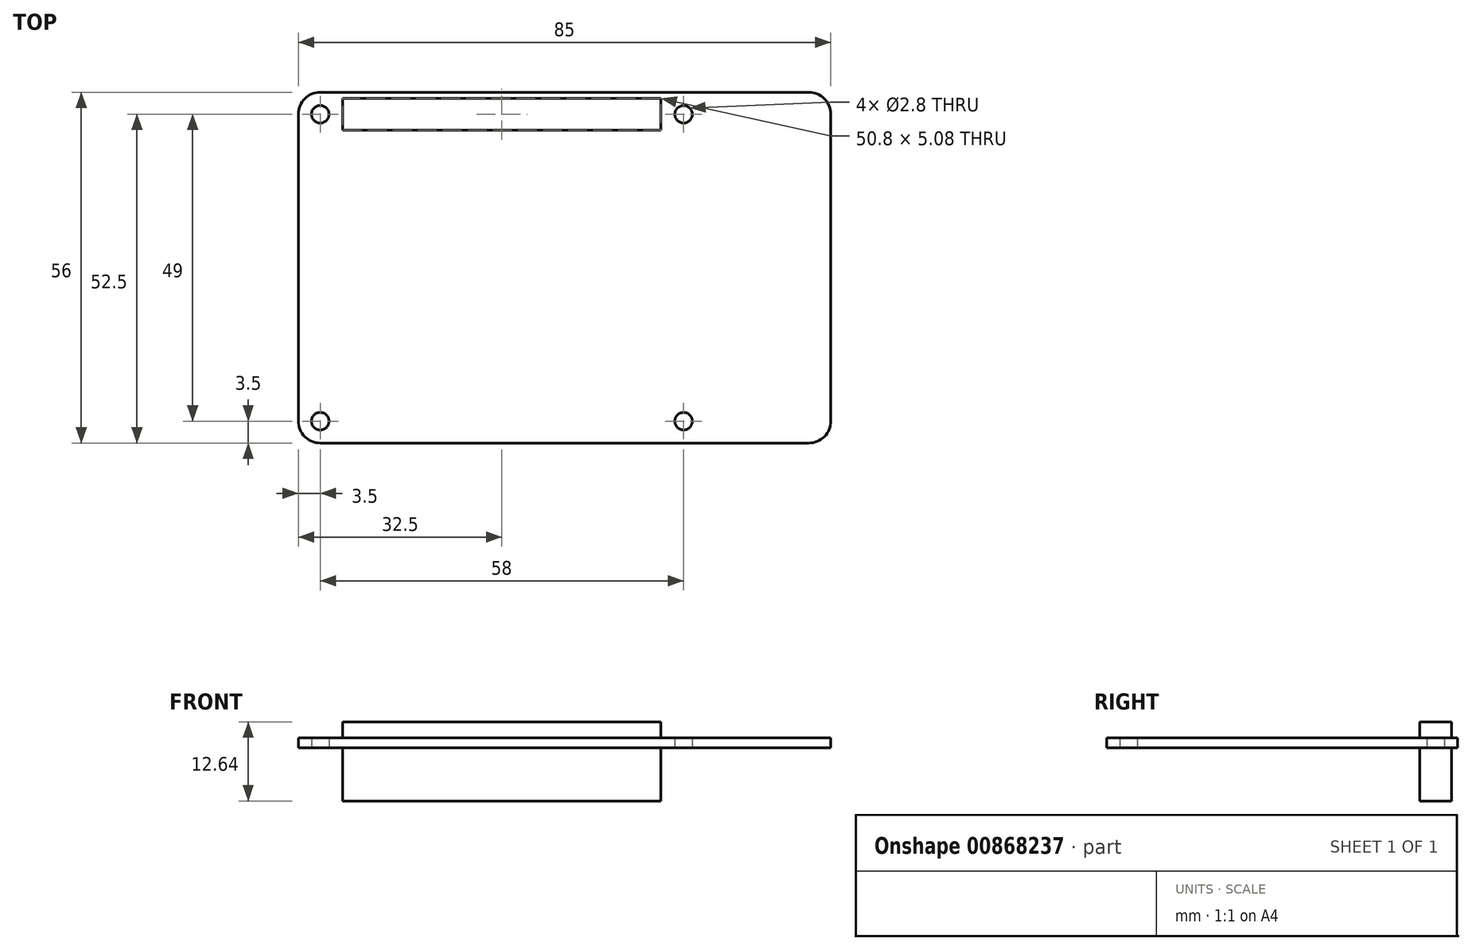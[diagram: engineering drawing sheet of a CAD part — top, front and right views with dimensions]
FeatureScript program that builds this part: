
annotation { "Feature Type Name" : "Feature", "Feature Type Description" : "" }
export const myFeature = defineFeature(function(context is Context, id is Id, definition is map)
    precondition{}
    {
        {
            var Q0;
            Q0=qCreatedBy(makeId("Top.planeOp"),FACE);
            var sketch = newSketch(context, id + "F0", { "sketchPlane" : qUnion([Q0])});
            skPoint(sketch, "E0.middle", {"position": v(0, 0) * mm});
            skLineSegment(sketch, "E1.bottom", {"start": v(29, -24.5) * mm, "end": v(-29, -24.5) * mm, "construction": true});
            skLineSegment(sketch, "E1.top", {"start": v(29, 24.5) * mm, "end": v(-29, 24.5) * mm, "construction": true});
            skLineSegment(sketch, "E1.left", {"start": v(29, -24.5) * mm, "end": v(29, 24.5) * mm, "construction": true});
            skLineSegment(sketch, "E1.right", {"start": v(-29, -24.5) * mm, "end": v(-29, 24.5) * mm, "construction": true});
            skLineSegment(sketch, "E2.bottom", {"start": v(-32.5, 28) * mm, "end": v(52.5, 28) * mm});
            skLineSegment(sketch, "E2.top", {"start": v(-32.5, -28) * mm, "end": v(52.5, -28) * mm});
            skLineSegment(sketch, "E2.left", {"start": v(-32.5, 28) * mm, "end": v(-32.5, -28) * mm});
            skLineSegment(sketch, "E2.right", {"start": v(52.5, 28) * mm, "end": v(52.5, -28) * mm});
            skSolve(sketch);
        }
        {
            var Q0;
            Q0=qSketchRegion(id+"F0",true);
            extrude(context, id + "F1", {"entities" : qUnion([Q0]), "depth" : 1.6 * mm, "offsetDistance" : 25 * mm});
        }
        {
            var Q0;
            Q0=sQuery(id+"F0.wireOp",VERTEX,"E1.top.end");
            var Q1;
            Q1=sQuery(id+"F0.wireOp",VERTEX,"E1.top.start");
            var Q2;
            Q2=sQuery(id+"F0.wireOp",VERTEX,"E1.bottom.start");
            var Q3;
            Q3=sQuery(id+"F0.wireOp",VERTEX,"E1.bottom.end");
            var Q4;
            Q4=makeQuery(id+"F1.opExtrude","SWEPT_BODY",BODY,{"disambiguationData":[OSD([sQuery(id+"F0.wireOp",EDGE,"E2.bottom"),sQuery(id+"F0.wireOp",EDGE,"E2.top"),sQuery(id+"F0.wireOp",EDGE,"E2.left"),sQuery(id+"F0.wireOp",EDGE,"E2.right")])]});
            hole(context, id + "F2", {"style" : HoleStyle.SIMPLE, "endStyle" : HoleEndStyle.THROUGH, "oppositeDirection" : true, "holeDiameter" : 2.8 * mm, "majorDiameter" : 5 * mm, "isTappedThrough" : true, "tappedDepth" : 12 * mm, "tapClearance" : 3, "locations" : qUnion([Q0, Q1, Q2, Q3]), "scope" : qUnion([Q4])});
        }
        {
            var Q0;
            Q0=makeQuery(id+"F1.opExtrude","CAP_FACE",FACE,{"disambiguationData":[OSD([sQuery(id+"F0.wireOp",EDGE,"E2.bottom"),sQuery(id+"F0.wireOp",EDGE,"E2.top"),sQuery(id+"F0.wireOp",EDGE,"E2.left"),sQuery(id+"F0.wireOp",EDGE,"E2.right")])],"isStart":true});
            var sketch = newSketch(context, id + "F3", { "sketchPlane" : qUnion([Q0])});
            skLineSegment(sketch, "E3", {"start": v(-29, -24.5) * mm, "end": v(29, -24.5) * mm, "construction": true});
            skLineSegment(sketch, "E4.bottom", {"start": v(25.4, -27.04) * mm, "end": v(-25.4, -27.04) * mm});
            skLineSegment(sketch, "E4.top", {"start": v(25.4, -21.96) * mm, "end": v(-25.4, -21.96) * mm});
            skLineSegment(sketch, "E4.left", {"start": v(25.4, -27.04) * mm, "end": v(25.4, -21.96) * mm});
            skLineSegment(sketch, "E4.right", {"start": v(-25.4, -27.04) * mm, "end": v(-25.4, -21.96) * mm});
            skPoint(sketch, "E4.middle", {"position": v(0, -24.5) * mm});
            skSolve(sketch);
        }
        {
            var Q0;
            Q0=makeQuery(id+"F3.imprint","IMPRINT",FACE,{"disambiguationData":[TD([[makeQuery(id+"F3.imprint","IMPRINT",EDGE,{"derivedFrom":sQuery(id+"F3.wireOp",EDGE,"E4.bottom")}),-1.0]])]});
            extrude(context, id + "F4", {"entities" : qUnion([Q0]), "operationType" : NewBodyOperationType.ADD, "depth" : 8.5 * mm, "offsetDistance" : 25 * mm});
        }
        {
            var Q0;
            Q0=makeQuery(id+"F3.imprint","IMPRINT",FACE,{"disambiguationData":[TD([[makeQuery(id+"F3.imprint","IMPRINT",EDGE,{"derivedFrom":sQuery(id+"F3.wireOp",EDGE,"E4.bottom")}),-1.0]])]});
            extrude(context, id + "F5", {"entities" : qUnion([Q0]), "operationType" : NewBodyOperationType.ADD, "oppositeDirection" : true, "depth" : (1.6 + 2.54) * mm, "offsetDistance" : 25 * mm});
        }
        {
            var Q0;
            Q0=makeQuery(id+"F1.opExtrude","SWEPT_EDGE",EDGE,{"disambiguationData":[OSD([sQuery(id+"F0.wireOp",EDGE,"E2.bottom"),sQuery(id+"F0.wireOp",EDGE,"E2.left")])]});
            var Q1;
            Q1=makeQuery(id+"F1.opExtrude","SWEPT_EDGE",EDGE,{"disambiguationData":[OSD([sQuery(id+"F0.wireOp",EDGE,"E2.top"),sQuery(id+"F0.wireOp",EDGE,"E2.left")])]});
            var Q2;
            Q2=makeQuery(id+"F1.opExtrude","SWEPT_EDGE",EDGE,{"disambiguationData":[OSD([sQuery(id+"F0.wireOp",EDGE,"E2.top"),sQuery(id+"F0.wireOp",EDGE,"E2.right")])]});
            var Q3;
            Q3=makeQuery(id+"F1.opExtrude","SWEPT_EDGE",EDGE,{"disambiguationData":[OSD([sQuery(id+"F0.wireOp",EDGE,"E2.bottom"),sQuery(id+"F0.wireOp",EDGE,"E2.right")])]});
            fillet(context, id + "F6", {"entities" : qUnion([Q0, Q1, Q2, Q3]), "radius" : 3.5 * mm, "tangentPropagation" : true, "allowEdgeOverflow" : false});
        }
    });
